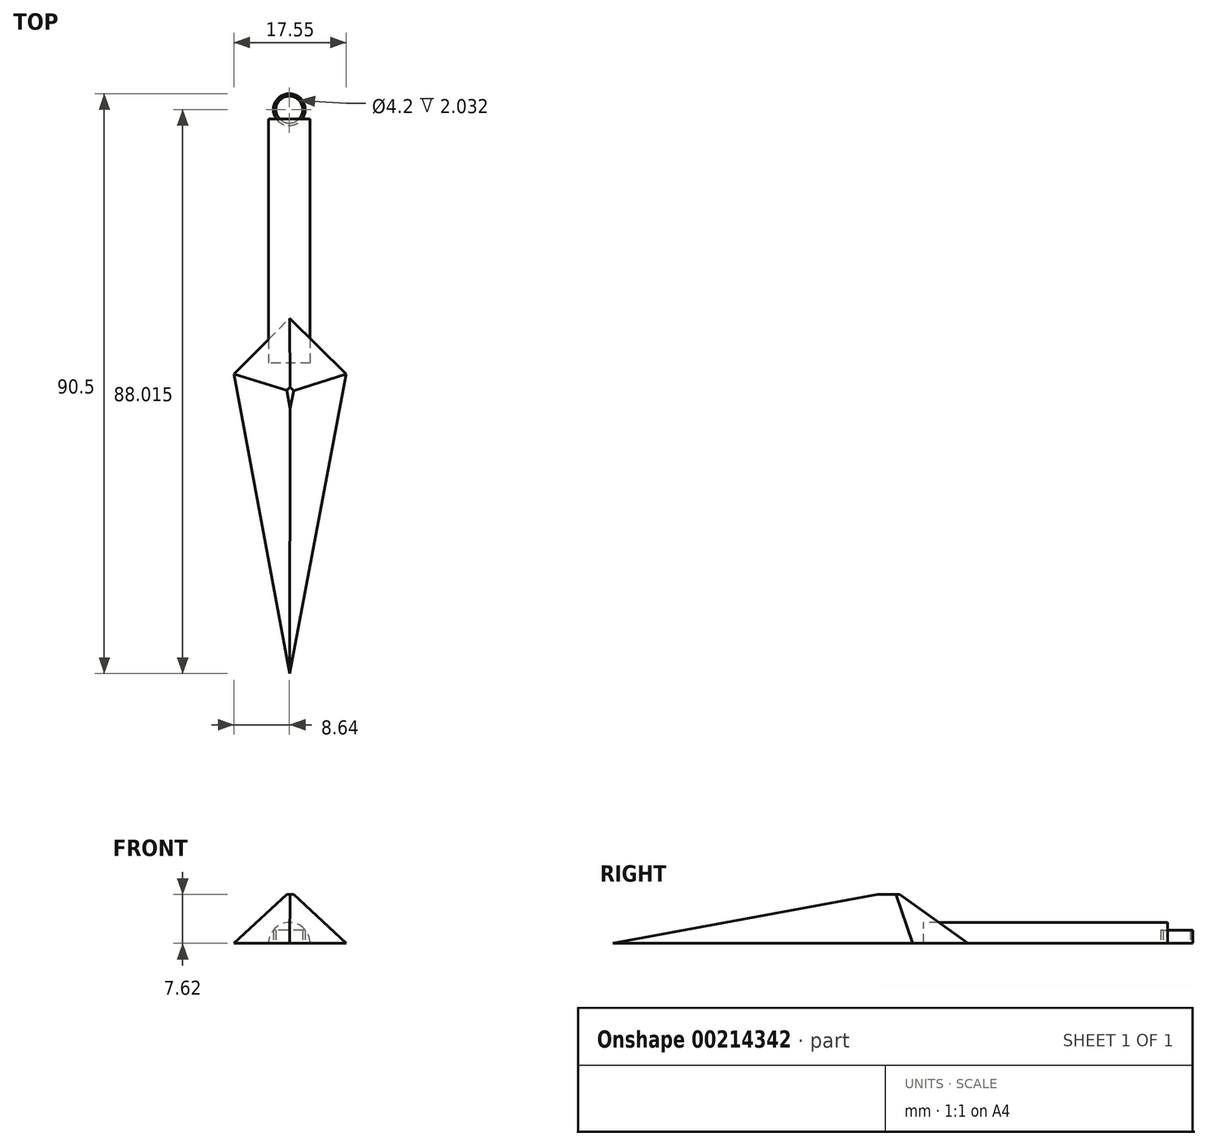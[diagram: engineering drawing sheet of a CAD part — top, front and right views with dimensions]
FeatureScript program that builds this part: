
annotation { "Feature Type Name" : "Feature", "Feature Type Description" : "" }
export const myFeature = defineFeature(function(context is Context, id is Id, definition is map)
    precondition{}
    {
        {
            var Q0;
            Q0=qCreatedBy(makeId("Top.planeOp"),FACE);
            var sketch = newSketch(context, id + "F0", { "sketchPlane" : qUnion([Q0])});
            skLineSegment(sketch, "E0", {"start": v(0, -76.02) * mm, "end": v(14.4, 0) * mm});
            skLineSegment(sketch, "E1", {"start": v(14.4, 0) * mm, "end": v(-14.12, 0) * mm});
            skLineSegment(sketch, "E2", {"start": v(-14.12, 0) * mm, "end": v(0, -76.02) * mm});
            skLineSegment(sketch, "E3", {"start": v(0, 14.12) * mm, "end": v(-14.12, 0) * mm});
            skLineSegment(sketch, "E4", {"start": v(14.4, 0) * mm, "end": v(0, 14.12) * mm});
            skLineSegment(sketch, "E5", {"start": v(0, 14.12) * mm, "end": v(0, -76.02) * mm});
            skSolve(sketch);
        }
        {
            var Q0;
            {var subQ0=sQuery(id+"F0.wireOp",EDGE,"E4");Q0=makeQuery(id+"F0.imprint","IMPRINT",FACE,{"disambiguationData":[TD([[makeQuery(id+"F0.imprint","IMPRINT",EDGE,{"derivedFrom":subQ0}),1.0]])]});}
            var Q1;
            {var subQ0=sQuery(id+"F0.wireOp",EDGE,"E3");Q1=makeQuery(id+"F0.imprint","IMPRINT",FACE,{"disambiguationData":[TD([[makeQuery(id+"F0.imprint","IMPRINT",EDGE,{"derivedFrom":subQ0}),1.0]])]});}
            var Q2;
            {var subQ0=sQuery(id+"F0.wireOp",EDGE,"E2");Q2=makeQuery(id+"F0.imprint","IMPRINT",FACE,{"disambiguationData":[TD([[makeQuery(id+"F0.imprint","IMPRINT",EDGE,{"derivedFrom":subQ0}),1.0]])]});}
            var Q3;
            {var subQ0=sQuery(id+"F0.wireOp",EDGE,"E0");Q3=makeQuery(id+"F0.imprint","IMPRINT",FACE,{"disambiguationData":[TD([[makeQuery(id+"F0.imprint","IMPRINT",EDGE,{"derivedFrom":subQ0}),1.0]])]});}
            extrude(context, id + "F1", {"entities" : qUnion([Q0, Q1, Q2, Q3]), "depth" : 7.62 * mm});
        }
        {
            var Q0;
            Q0=makeQuery(id+"F1.opExtrude","CAP_FACE",FACE,{"disambiguationData":[OSD([sQuery(id+"F0.wireOp",EDGE,"E0"),sQuery(id+"F0.wireOp",EDGE,"E2"),sQuery(id+"F0.wireOp",EDGE,"E3"),sQuery(id+"F0.wireOp",EDGE,"E4")])],"isStart":false});
            chamfer(context, id + "F2", {"entities" : qUnion([Q0]), "width" : 12.7 * mm, "tangentPropagation" : true});
        }
        {
            var Q0;
            Q0=qCreatedBy(makeId("Top.planeOp"),FACE);
            var sketch = newSketch(context, id + "F3", { "sketchPlane" : qUnion([Q0])});
            skCircle(sketch, "E6", {"center": v(0, 39.55) * mm, "radius": 2.49 * mm});
            skCircle(sketch, "E7", {"center": v(0, 39.55) * mm, "radius": 2.1 * mm});
            skSolve(sketch);
        }
        {
            var Q0;
            Q0=makeQuery(id+"F3.imprint","IMPRINT",FACE,{"disambiguationData":[TD([[makeQuery(id+"F3.imprint","IMPRINT",EDGE,{"derivedFrom":sQuery(id+"F3.wireOp",EDGE,"E6")}),1.0]])]});
            extrude(context, id + "F4", {"entities" : qUnion([Q0]), "operationType" : NewBodyOperationType.ADD, "depth" : 2.03 * mm});
        }
        {
            var Q0;
            Q0=qCreatedBy(makeId("Front.planeOp"),FACE);
            var sketch = newSketch(context, id + "F5", { "sketchPlane" : qUnion([Q0])});
            skArc(sketch, "E8", {"start": v(3.26, 0) * mm, "mid": v(0, 3.26) * mm, "end": v(-3.26, 0) * mm});
            skLineSegment(sketch, "E9", {"start": v(3.26, 0) * mm, "end": v(-3.26, 0) * mm});
            skSolve(sketch);
        }
        {
            var Q0;
            Q0 = qSketchRegion(id + "F5", true);
            extrude(context, id + "F6", {"entities" : qUnion([Q0]), "oppositeDirection" : true, "depth" : 38.1 * mm});
        }
    });
